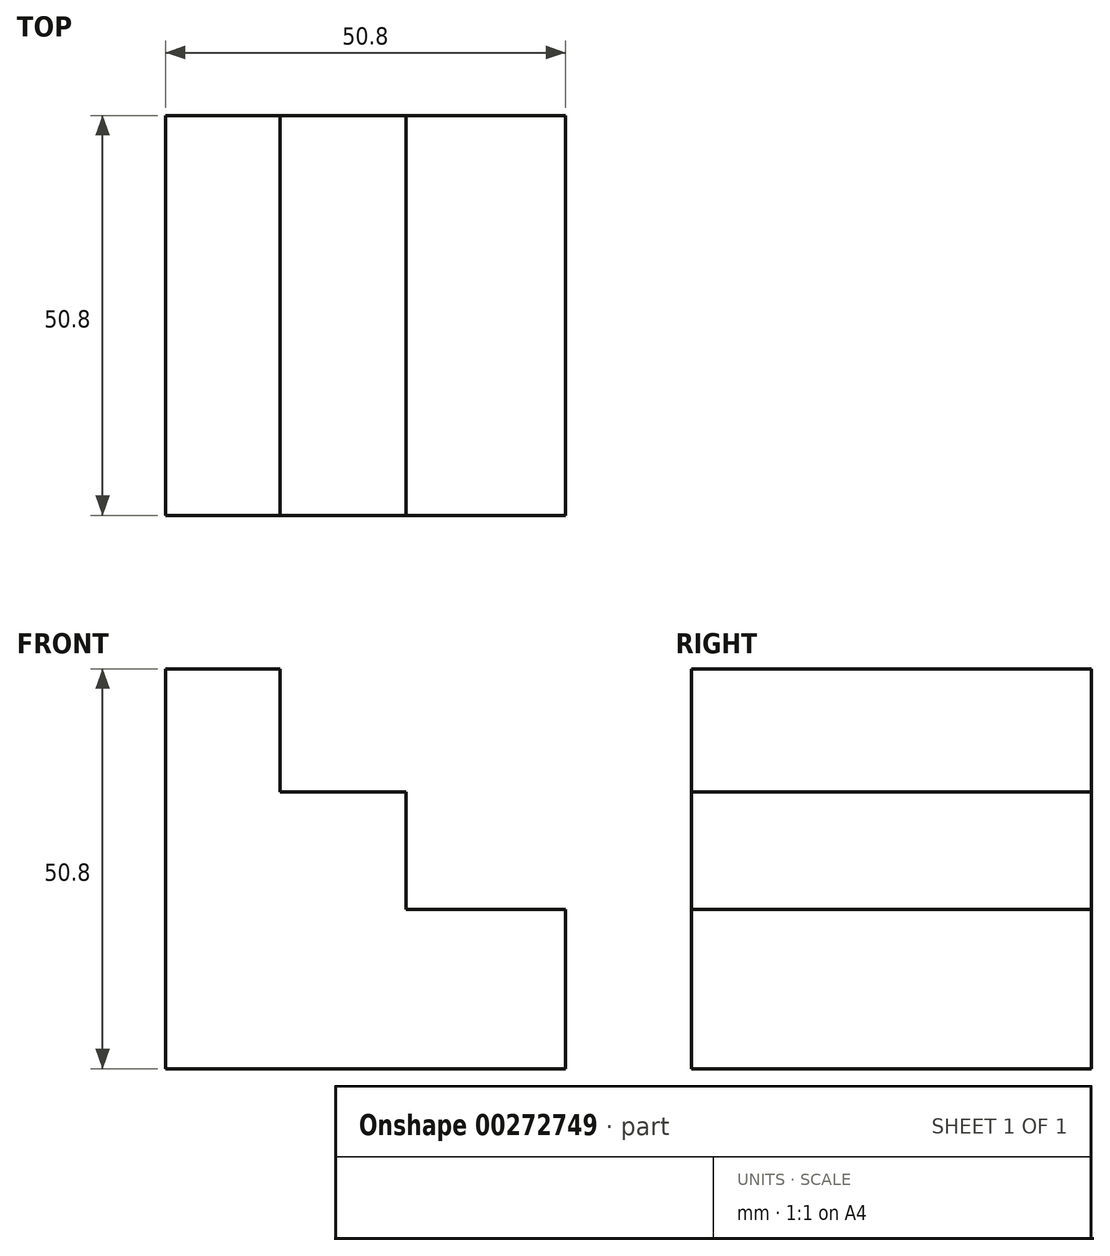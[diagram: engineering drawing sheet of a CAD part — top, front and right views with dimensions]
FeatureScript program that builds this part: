
annotation { "Feature Type Name" : "Feature", "Feature Type Description" : "" }
export const myFeature = defineFeature(function(context is Context, id is Id, definition is map)
    precondition{}
    {
        {
            var Q0;
            Q0=qCreatedBy(makeId("Front.planeOp"),FACE);
            var sketch = newSketch(context, id + "F0", { "sketchPlane" : qUnion([Q0])});
            skLineSegment(sketch, "E0", {"start": v(0, 0) * mm, "end": v(-50.8, 0) * mm});
            skLineSegment(sketch, "E1", {"start": v(-50.8, 0) * mm, "end": v(-50.8, 50.8) * mm});
            skLineSegment(sketch, "E2", {"start": v(-50.8, 50.8) * mm, "end": v(-36.28, 50.8) * mm});
            skLineSegment(sketch, "E3", {"start": v(-36.28, 50.8) * mm, "end": v(-36.28, 35.14) * mm});
            skLineSegment(sketch, "E4", {"start": v(-36.28, 35.14) * mm, "end": v(-20.24, 35.14) * mm});
            skLineSegment(sketch, "E5", {"start": v(-20.24, 35.14) * mm, "end": v(-20.24, 20.24) * mm});
            skLineSegment(sketch, "E6", {"start": v(-20.24, 20.24) * mm, "end": v(0, 20.24) * mm});
            skLineSegment(sketch, "E7", {"start": v(0, 20.24) * mm, "end": v(0, 0) * mm});
            skSolve(sketch);
        }
        {
            var Q0;
            Q0=makeQuery(id+"F0.imprint","IMPRINT",FACE,{"disambiguationData":[TD([[makeQuery(id+"F0.imprint","IMPRINT",EDGE,{"derivedFrom":sQuery(id+"F0.wireOp",EDGE,"E0")}),-1.0]])]});
            extrude(context, id + "F1", {"entities" : qUnion([Q0]), "depth" : 50.8 * mm});
        }
    });
